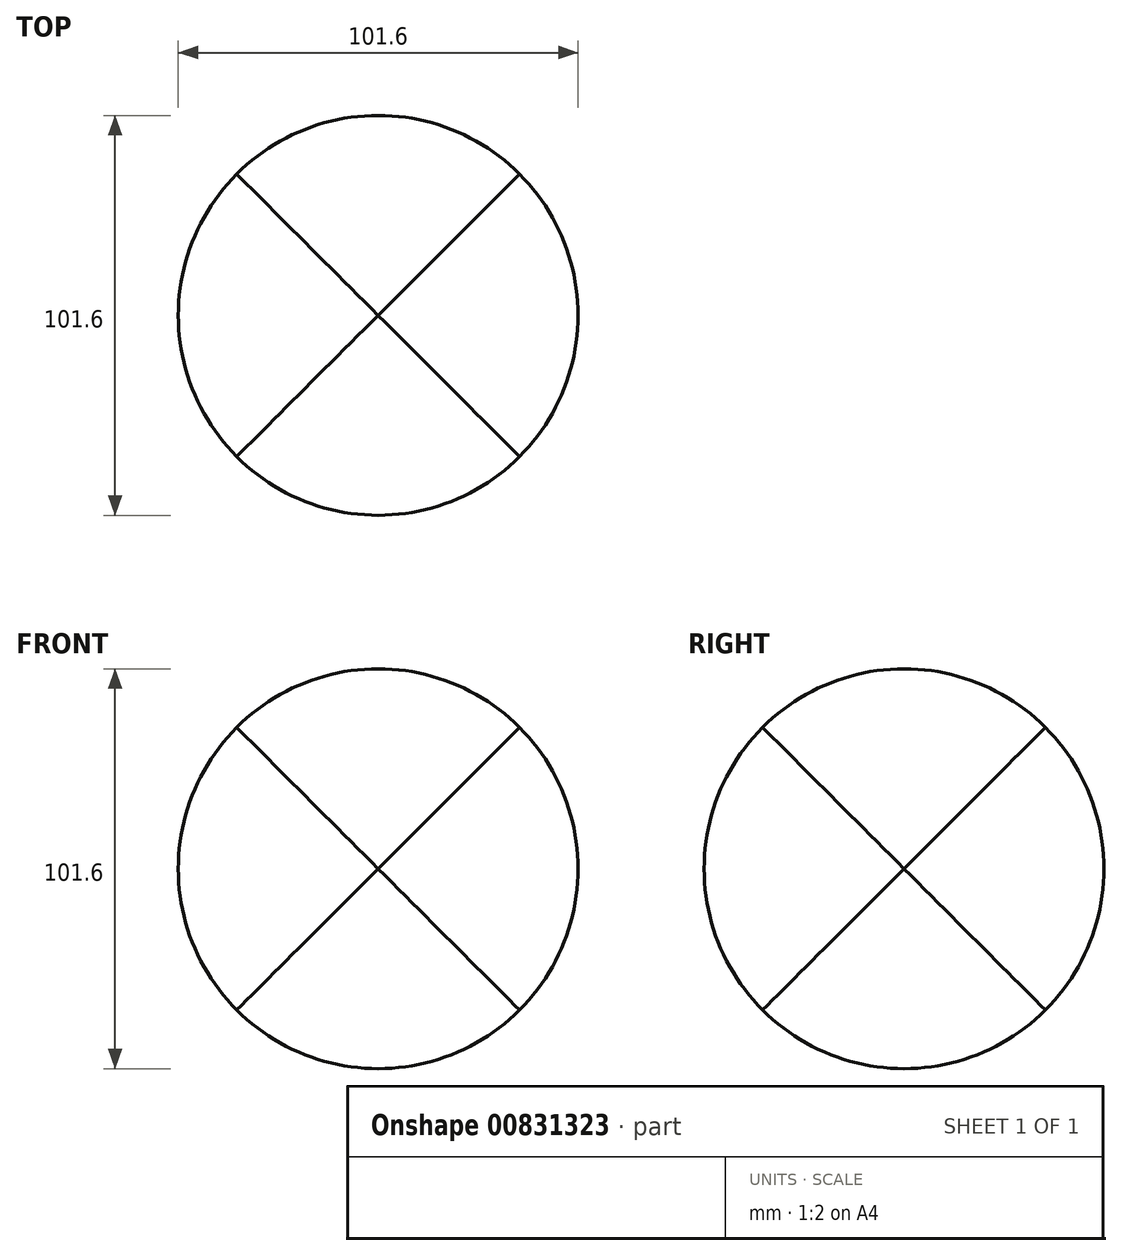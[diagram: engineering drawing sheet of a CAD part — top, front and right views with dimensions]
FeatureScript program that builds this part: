
annotation { "Feature Type Name" : "Feature", "Feature Type Description" : "" }
export const myFeature = defineFeature(function(context is Context, id is Id, definition is map)
    precondition{}
    {
        {
            var Q0;
            Q0=qCreatedBy(makeId("Top.planeOp"),FACE);
            var sketch = newSketch(context, id + "F0", { "sketchPlane" : qUnion([Q0])});
            skCircle(sketch, "E0", {"center": v(0, 0) * mm, "radius": 50.8 * mm});
            skSolve(sketch);
        }
        {
            var Q0;
            Q0=makeQuery(id+"F0.imprint","IMPRINT",FACE,{"disambiguationData":[TD([[makeQuery(id+"F0.imprint","IMPRINT",EDGE,{"derivedFrom":sQuery(id+"F0.wireOp",EDGE,"E0")}),1.0]])]});
            extrude(context, id + "F1", {"entities" : qUnion([Q0]), "depth" : 50.8 * mm, "offsetDistance" : 25.4 * mm, "hasSecondDirection" : true, "secondDirectionOppositeDirection" : true, "secondDirectionDepth" : 50.8 * mm});
        }
        {
            var Q0;
            Q0=qCreatedBy(makeId("Front.planeOp"),FACE);
            var sketch = newSketch(context, id + "F2", { "sketchPlane" : qUnion([Q0])});
            skCircle(sketch, "E1", {"center": v(0, 0) * mm, "radius": 50.8 * mm});
            skSolve(sketch);
        }
        {
            var Q0;
            Q0=qCreatedBy(makeId("Right.planeOp"),FACE);
            var sketch = newSketch(context, id + "F3", { "sketchPlane" : qUnion([Q0])});
            skCircle(sketch, "E2", {"center": v(0, 0) * mm, "radius": 50.8 * mm});
            skSolve(sketch);
        }
        {
            var Q0;
            Q0 = qSketchRegion(id + "F2", true);
            extrude(context, id + "F4", {"entities" : qUnion([Q0]), "operationType" : NewBodyOperationType.INTERSECT, "depth" : 50.8 * mm, "offsetDistance" : 25.4 * mm, "hasSecondDirection" : true, "secondDirectionOppositeDirection" : true, "secondDirectionDepth" : 50.8 * mm});
        }
        {
            var Q0;
            Q0 = qSketchRegion(id + "F3", true);
            extrude(context, id + "F5", {"entities" : qUnion([Q0]), "operationType" : NewBodyOperationType.INTERSECT, "depth" : 50.8 * mm, "offsetDistance" : 25.4 * mm, "hasSecondDirection" : true, "secondDirectionOppositeDirection" : true, "secondDirectionDepth" : 50.8 * mm});
        }
    });
